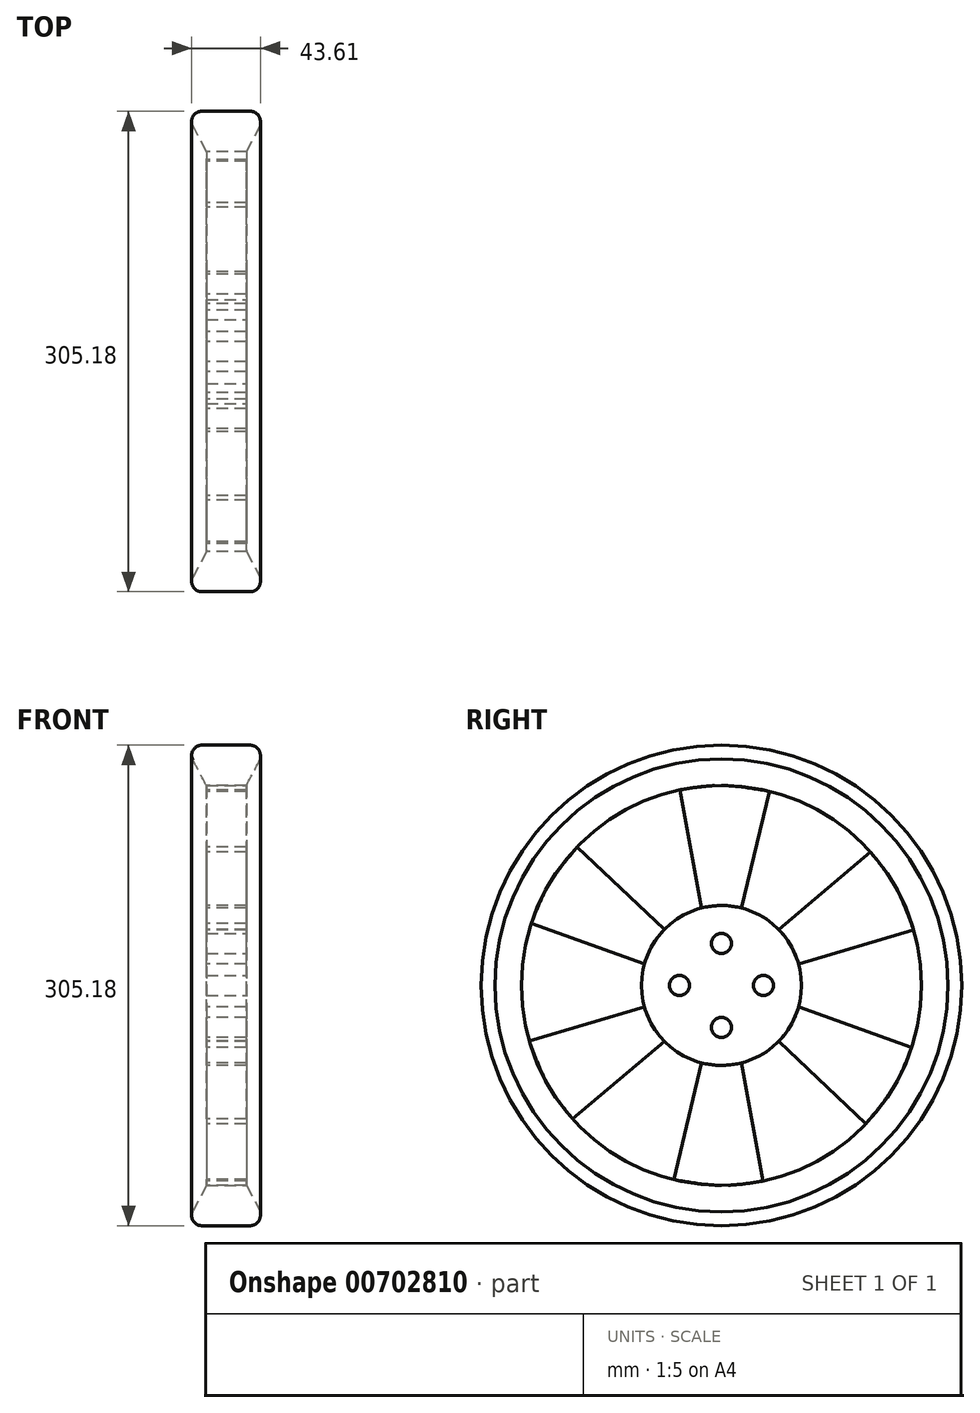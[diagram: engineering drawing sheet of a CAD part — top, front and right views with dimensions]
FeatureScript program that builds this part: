
annotation { "Feature Type Name" : "Feature", "Feature Type Description" : "" }
export const myFeature = defineFeature(function(context is Context, id is Id, definition is map)
    precondition{}
    {
        {
            var Q0;
            Q0=qCreatedBy(makeId("Front.planeOp"),FACE);
            var sketch = newSketch(context, id + "F0", { "sketchPlane" : qUnion([Q0])});
            skLineSegment(sketch, "E0", {"start": v(-15.67, 152.6) * mm, "end": v(15.24, 152.6) * mm});
            skLineSegment(sketch, "E1", {"start": v(21.59, 146.24) * mm, "end": v(21.59, 143.85) * mm});
            skLineSegment(sketch, "E2", {"start": v(21.59, 143.85) * mm, "end": v(12.7, 127) * mm});
            skLineSegment(sketch, "E3", {"start": v(12.7, 127) * mm, "end": v(-12.7, 127) * mm});
            skLineSegment(sketch, "E4", {"start": v(-12.7, 127) * mm, "end": v(-21.3, 143.28) * mm});
            skPoint(sketch, "E5.newPointB", {"position": v(-21.59, 143.85) * mm});
            skArc(sketch, "E5.filletArc", {"start": v(-15.67, 152.6) * mm, "mid": v(-21.11, 149.52) * mm, "end": v(-21.3, 143.28) * mm});
            skPoint(sketch, "E6.visualSharp", {"position": v(21.59, 152.6) * mm});
            skArc(sketch, "E6.filletArc", {"start": v(21.59, 146.24) * mm, "mid": v(19.73, 150.73) * mm, "end": v(15.24, 152.6) * mm});
            skSolve(sketch);
        }
        {
            var Q0;
            Q0=qCreatedBy(makeId("Front.planeOp"),FACE);
            var sketch = newSketch(context, id + "F1", { "sketchPlane" : qUnion([Q0])});
            skLineSegment(sketch, "E7", {"start": v(-28.69, 0) * mm, "end": v(35.13, 0) * mm, "construction": true});
            skSolve(sketch);
        }
        {
            var Q0;
            Q0=qCreatedBy(makeId("Right.planeOp"),FACE);
            var sketch = newSketch(context, id + "F2", { "sketchPlane" : qUnion([Q0])});
            skCircle(sketch, "E8", {"center": v(0, 0) * mm, "radius": 50.8 * mm});
            skSolve(sketch);
        }
        {
            var Q0;
            Q0 = qSketchRegion(id + "F0", true);
            var Q1;
            Q1=sQuery(id+"F1.wireOp",EDGE,"E7");
            revolve(context, id + "F3", {"surfaceOperationType" : NewSurfaceOperationType.NEW, "entities" : qUnion([Q0]), "axis" : qUnion([Q1]), "revolveType" : RevolveType.FULL});
        }
        {
            var Q0;
            Q0=qCreatedBy(makeId("Right.planeOp"),FACE);
            var sketch = newSketch(context, id + "F4", { "sketchPlane" : qUnion([Q0])});
            skPoint(sketch, "E9", {"position": v(0, -50.8) * mm});
            skLineSegment(sketch, "E10", {"start": v(12.7, -49.3) * mm, "end": v(26.24, -124.26) * mm});
            skLineSegment(sketch, "E11", {"start": v(-12.7, -49.3) * mm, "end": v(-30.33, -123.32) * mm});
            skFitSpline(sketch, "E12", {"points": [v(12.7, -49.3) * mm, v(0, -50.8) * mm, v(-12.7, -49.3) * mm], "startDerivative": vector(-29.03, -5.28) * mm, "endDerivative": vector(-30.45, 5.5) * mm});
            skFitSpline(sketch, "E13", {"points": [v(26.24, -124.26) * mm, v(0, -127) * mm, v(-30.33, -123.32) * mm], "startDerivative": vector(-53.5, -8.77) * mm, "endDerivative": vector(-59.57, 10.4) * mm});
            skSolve(sketch);
        }
        {
            var Q0;
            Q0 = qSketchRegion(id + "F4", true);
            extrude(context, id + "F5", {"entities" : qUnion([Q0]), "endBound" : BoundingType.SYMMETRIC, "depth" : 25.4 * mm, "offsetDistance" : 25.4 * mm});
        }
        {
            var Q0;
            Q0=makeQuery(id+"F5.opExtrude","SWEPT_BODY",BODY,{"disambiguationData":[OSD([sQuery(id+"F4.wireOp",EDGE,"E10"),sQuery(id+"F4.wireOp",EDGE,"E11"),sQuery(id+"F4.wireOp",EDGE,"E12"),sQuery(id+"F4.wireOp",EDGE,"E13")])]});
            var Q1;
            Q1=sQuery(id+"F2.wireOp",EDGE,"E8");
            circularPattern(context, id + "F6", {"entities" : qUnion([Q0]), "axis" : qUnion([Q1]), "angle" : 360 * degree, "instanceCount" : 6, "equalSpace" : true});
        }
        {
            var Q0;
            Q0=qCreatedBy(makeId("Right.planeOp"),FACE);
            var sketch = newSketch(context, id + "F7", { "sketchPlane" : qUnion([Q0])});
            skCircle(sketch, "E14", {"center": v(0, 0) * mm, "radius": 50.8 * mm});
            skSolve(sketch);
        }
        {
            var Q0;
            Q0 = qSketchRegion(id + "F7", true);
            extrude(context, id + "F8", {"entities" : qUnion([Q0]), "endBound" : BoundingType.SYMMETRIC, "depth" : 25.4 * mm, "offsetDistance" : 25.4 * mm});
        }
        {
            var Q0;
            Q0=qCreatedBy(makeId("Right.planeOp"),FACE);
            var sketch = newSketch(context, id + "F9", { "sketchPlane" : qUnion([Q0])});
            skCircle(sketch, "E15", {"center": v(0, -26.67) * mm, "radius": 6.35 * mm});
            skSolve(sketch);
        }
        {
            var Q0;
            Q0 = qSketchRegion(id + "F9", true);
            extrude(context, id + "F10", {"entities" : qUnion([Q0]), "operationType" : NewBodyOperationType.REMOVE, "endBound" : BoundingType.SYMMETRIC, "depth" : 50.8 * mm, "offsetDistance" : 25.4 * mm});
        }
        {
            var Q0;
            Q0=qCreatedBy(makeId("Right.planeOp"),FACE);
            var sketch = newSketch(context, id + "F11", { "sketchPlane" : qUnion([Q0])});
            skCircle(sketch, "E16", {"center": v(0, 26.67) * mm, "radius": 6.35 * mm});
            skCircle(sketch, "E17", {"center": v(-26.67, 0) * mm, "radius": 6.35 * mm});
            skCircle(sketch, "E18", {"center": v(26.67, 0) * mm, "radius": 6.35 * mm});
            skSolve(sketch);
        }
        {
            var Q0;
            Q0 = qSketchRegion(id + "F11", true);
            extrude(context, id + "F12", {"entities" : qUnion([Q0]), "operationType" : NewBodyOperationType.REMOVE, "endBound" : BoundingType.SYMMETRIC, "oppositeDirection" : true, "depth" : 50.8 * mm, "offsetDistance" : 25.4 * mm});
        }
    });
